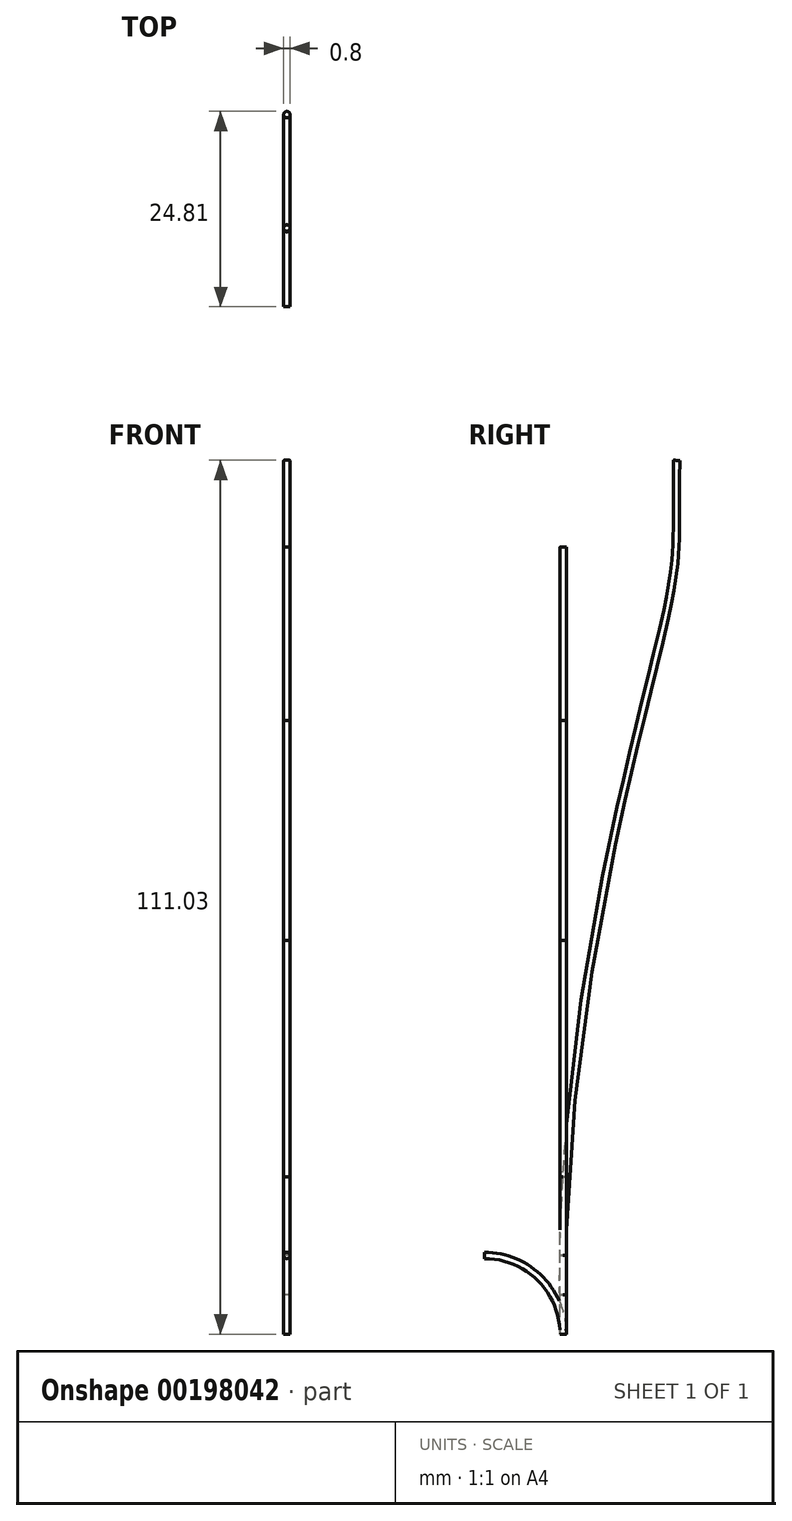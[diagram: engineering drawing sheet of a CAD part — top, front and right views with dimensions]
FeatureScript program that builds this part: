
annotation { "Feature Type Name" : "Feature", "Feature Type Description" : "" }
export const myFeature = defineFeature(function(context is Context, id is Id, definition is map)
    precondition{}
    {
        {
            var Q0;
            Q0=qCreatedBy(makeId("Right.planeOp"),FACE);
            var sketch = newSketch(context, id + "F0", { "sketchPlane" : qUnion([Q0])});
            skLineSegment(sketch, "E0", {"start": v(0, 0) * mm, "end": v(0, 77.99) * mm});
            skLineSegment(sketch, "E1", {"start": v(0, 0) * mm, "end": v(0, 20) * mm});
            skLineSegment(sketch, "E2", {"start": v(0, 0) * mm, "end": v(0, 50) * mm});
            skLineSegment(sketch, "E3", {"start": v(0, 0) * mm, "end": v(0, 100) * mm});
            skLineSegment(sketch, "E4", {"start": v(0, 0) * mm, "end": v(0, 10) * mm});
            skLineSegment(sketch, "E5", {"start": v(0, 0) * mm, "end": v(-10, 0) * mm, "construction": true});
            skArc(sketch, "E6", {"start": v(0, 0) * mm, "mid": v(-2.93, 7.07) * mm, "end": v(-10, 10) * mm});
            skLineSegment(sketch, "E7", {"start": v(0, 0) * mm, "end": v(0, 5) * mm});
            skFitSpline(sketch, "E8", {"points": [v(0, 0) * mm, v(13.42, 93.19) * mm, v(14.41, 111) * mm], "startDerivative": vector(-5.73, 179.2) * mm, "endDerivative": vector(1.1, 89.71) * mm});
            skSolve(sketch);
        }
        {
            var Q0;
            Q0=qCreatedBy(makeId("Top.planeOp"),FACE);
            var sketch = newSketch(context, id + "F1", { "sketchPlane" : qUnion([Q0])});
            skCircle(sketch, "E9", {"center": v(0, 0) * mm, "radius": 0.4 * mm});
            skSolve(sketch);
        }
        {
            var Q0;
            Q0=makeQuery(id+"F1.imprint","IMPRINT",FACE,{"disambiguationData":[TD([[makeQuery(id+"F1.imprint","IMPRINT",EDGE,{"derivedFrom":sQuery(id+"F1.wireOp",EDGE,"E9")}),1.0]])]});
            var Q1;
            Q1=sQuery(id+"F0.wireOp",EDGE,"E0");
            sweep(context, id + "F2", {"profiles" : qUnion([Q0]), "path" : qUnion([Q1])});
        }
        {
            var Q0;
            Q0=makeQuery(id+"F1.imprint","IMPRINT",FACE,{"disambiguationData":[TD([[makeQuery(id+"F1.imprint","IMPRINT",EDGE,{"derivedFrom":sQuery(id+"F1.wireOp",EDGE,"E9")}),1.0]])]});
            var Q1;
            Q1=sQuery(id+"F0.wireOp",EDGE,"E4");
            sweep(context, id + "F3", {"profiles" : qUnion([Q0]), "path" : qUnion([Q1])});
        }
        {
            var Q0;
            Q0=makeQuery(id+"F1.imprint","IMPRINT",FACE,{"disambiguationData":[TD([[makeQuery(id+"F1.imprint","IMPRINT",EDGE,{"derivedFrom":sQuery(id+"F1.wireOp",EDGE,"E9")}),1.0]])]});
            var Q1;
            Q1=sQuery(id+"F0.wireOp",EDGE,"E1");
            sweep(context, id + "F4", {"profiles" : qUnion([Q0]), "path" : qUnion([Q1])});
        }
        {
            var Q0;
            Q0=makeQuery(id+"F1.imprint","IMPRINT",FACE,{"disambiguationData":[TD([[makeQuery(id+"F1.imprint","IMPRINT",EDGE,{"derivedFrom":sQuery(id+"F1.wireOp",EDGE,"E9")}),1.0]])]});
            var Q1;
            Q1=sQuery(id+"F0.wireOp",EDGE,"E2");
            sweep(context, id + "F5", {"profiles" : qUnion([Q0]), "path" : qUnion([Q1])});
        }
        {
            var Q0;
            Q0=makeQuery(id+"F1.imprint","IMPRINT",FACE,{"disambiguationData":[TD([[makeQuery(id+"F1.imprint","IMPRINT",EDGE,{"derivedFrom":sQuery(id+"F1.wireOp",EDGE,"E9")}),1.0]])]});
            var Q1;
            Q1=sQuery(id+"F0.wireOp",EDGE,"E3");
            sweep(context, id + "F6", {"profiles" : qUnion([Q0]), "path" : qUnion([Q1])});
        }
        {
            var Q0;
            Q0=makeQuery(id+"F1.imprint","IMPRINT",FACE,{"disambiguationData":[TD([[makeQuery(id+"F1.imprint","IMPRINT",EDGE,{"derivedFrom":sQuery(id+"F1.wireOp",EDGE,"E9")}),1.0]])]});
            var Q1;
            Q1=sQuery(id+"F0.wireOp",EDGE,"E6");
            sweep(context, id + "F7", {"profiles" : qUnion([Q0]), "path" : qUnion([Q1])});
        }
        {
            var Q0;
            Q0=makeQuery(id+"F1.imprint","IMPRINT",FACE,{"disambiguationData":[TD([[makeQuery(id+"F1.imprint","IMPRINT",EDGE,{"derivedFrom":sQuery(id+"F1.wireOp",EDGE,"E9")}),1.0]])]});
            var Q1;
            Q1=sQuery(id+"F0.wireOp",EDGE,"E7");
            sweep(context, id + "F8", {"profiles" : qUnion([Q0]), "path" : qUnion([Q1])});
        }
        {
            var Q0;
            Q0=makeQuery(id+"F1.imprint","IMPRINT",FACE,{"disambiguationData":[TD([[makeQuery(id+"F1.imprint","IMPRINT",EDGE,{"derivedFrom":sQuery(id+"F1.wireOp",EDGE,"E9")}),1.0]])]});
            var Q1;
            Q1=sQuery(id+"F0.wireOp",EDGE,"E8");
            sweep(context, id + "F9", {"profiles" : qUnion([Q0]), "path" : qUnion([Q1])});
        }
    });
